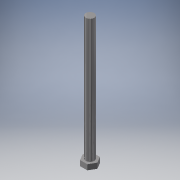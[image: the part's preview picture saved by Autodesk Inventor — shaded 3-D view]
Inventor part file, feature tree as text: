
AUTODESK INVENTOR PART (.ipt)
format: ipt  version: 2016 (Build 200138000, 138)  size: 117,248 bytes
history: native  units: in
note: dims shown in document units (in); Inventor stores cm internally (conversion verified against a paired STEP export)
features: extrude x2, sketch x2
ambient origin geometry x8: Origin, YZ Plane, XZ Plane, XY Plane, X Axis, Y Axis, Z Axis, Center Point
bodies: Solid1 (feature_tree)
feature tree (4):
  extrude  "Extrusion1"  Depth=0.2344in TaperAngle=0.0deg
  extrude  "Extrusion2"  Depth=5.5in TaperAngle=0.0deg
  sketch  "Sketch1"  dims[d0=0.5625in d1=0.2344in d2=0.0in]
  sketch  "Sketch2"  dims[d3=0.375in d4=5.5in d5=0.0in]
